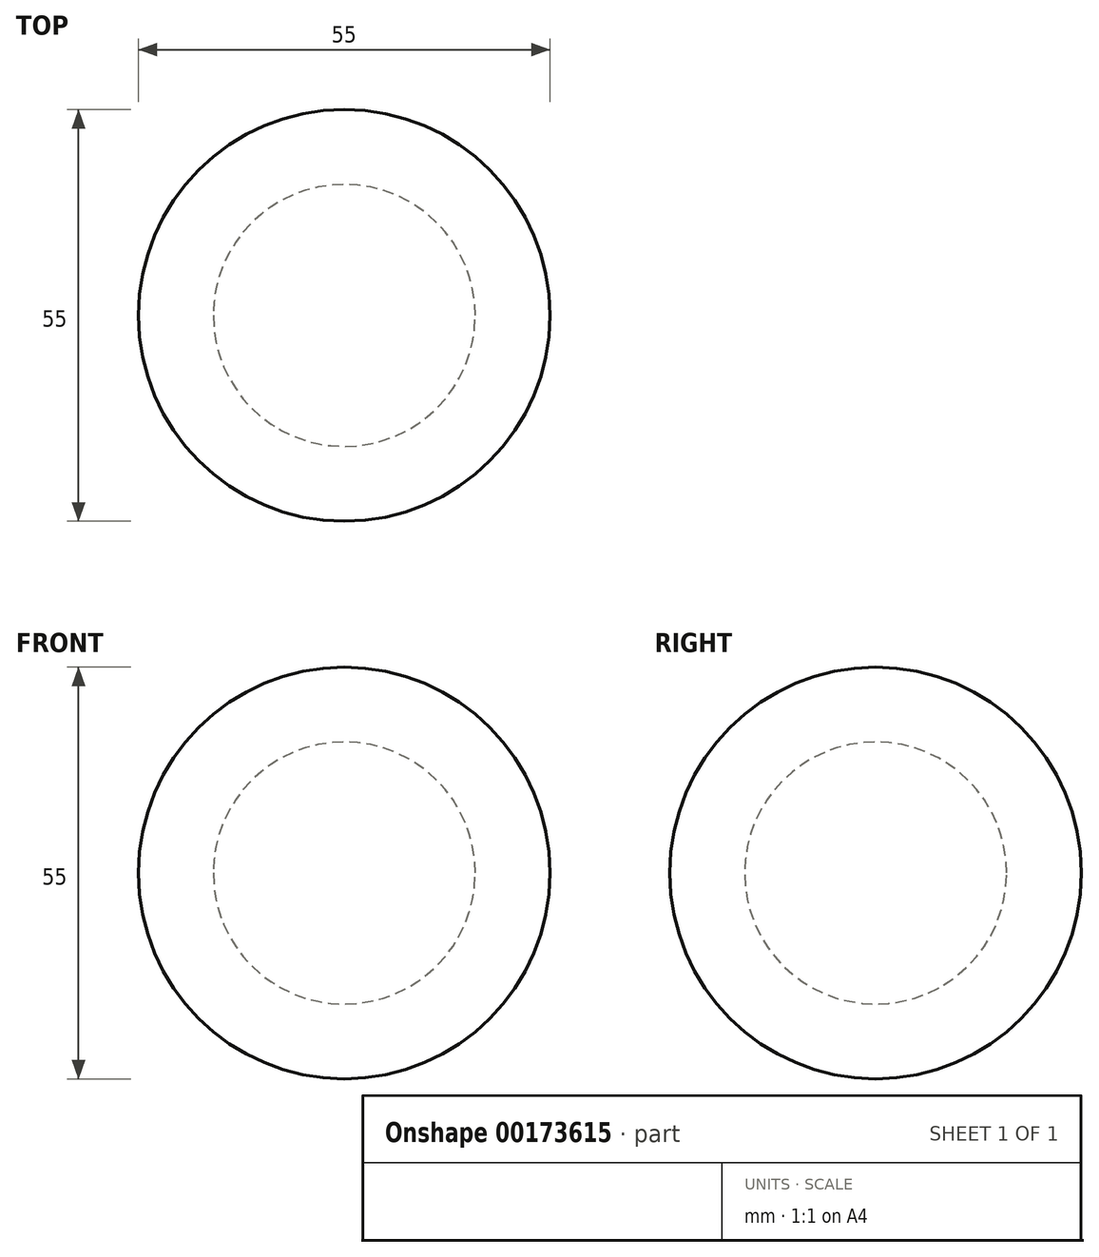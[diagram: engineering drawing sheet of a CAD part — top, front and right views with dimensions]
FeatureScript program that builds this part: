
annotation { "Feature Type Name" : "Feature", "Feature Type Description" : "" }
export const myFeature = defineFeature(function(context is Context, id is Id, definition is map)
    precondition{}
    {
        {
            var Q0;
            Q0=qCreatedBy(makeId("Front.planeOp"),FACE);
            var sketch = newSketch(context, id + "F0", { "sketchPlane" : qUnion([Q0])});
            skArc(sketch, "E0", {"start": v(-5.35, 21.26) * mm, "mid": v(-32.85, 48.76) * mm, "end": v(-60.35, 21.26) * mm});
            skArc(sketch, "E1", {"start": v(-15.35, 21.26) * mm, "mid": v(-32.85, 38.76) * mm, "end": v(-50.35, 21.26) * mm});
            skLineSegment(sketch, "E2", {"start": v(-60.35, 21.26) * mm, "end": v(-50.35, 21.26) * mm});
            skLineSegment(sketch, "E3.trimOffspring", {"start": v(-15.35, 21.26) * mm, "end": v(-5.35, 21.26) * mm});
            skSolve(sketch);
        }
        {
            var Q0;
            Q0 = qSketchRegion(id + "F0", true);
            var Q1;
            Q1=sQuery(id+"F0.wireOp",EDGE,"E3.trimOffspring");
            revolve(context, id + "F1", {"entities" : qUnion([Q0]), "axis" : qUnion([Q1]), "revolveType" : RevolveType.FULL});
        }
    });
